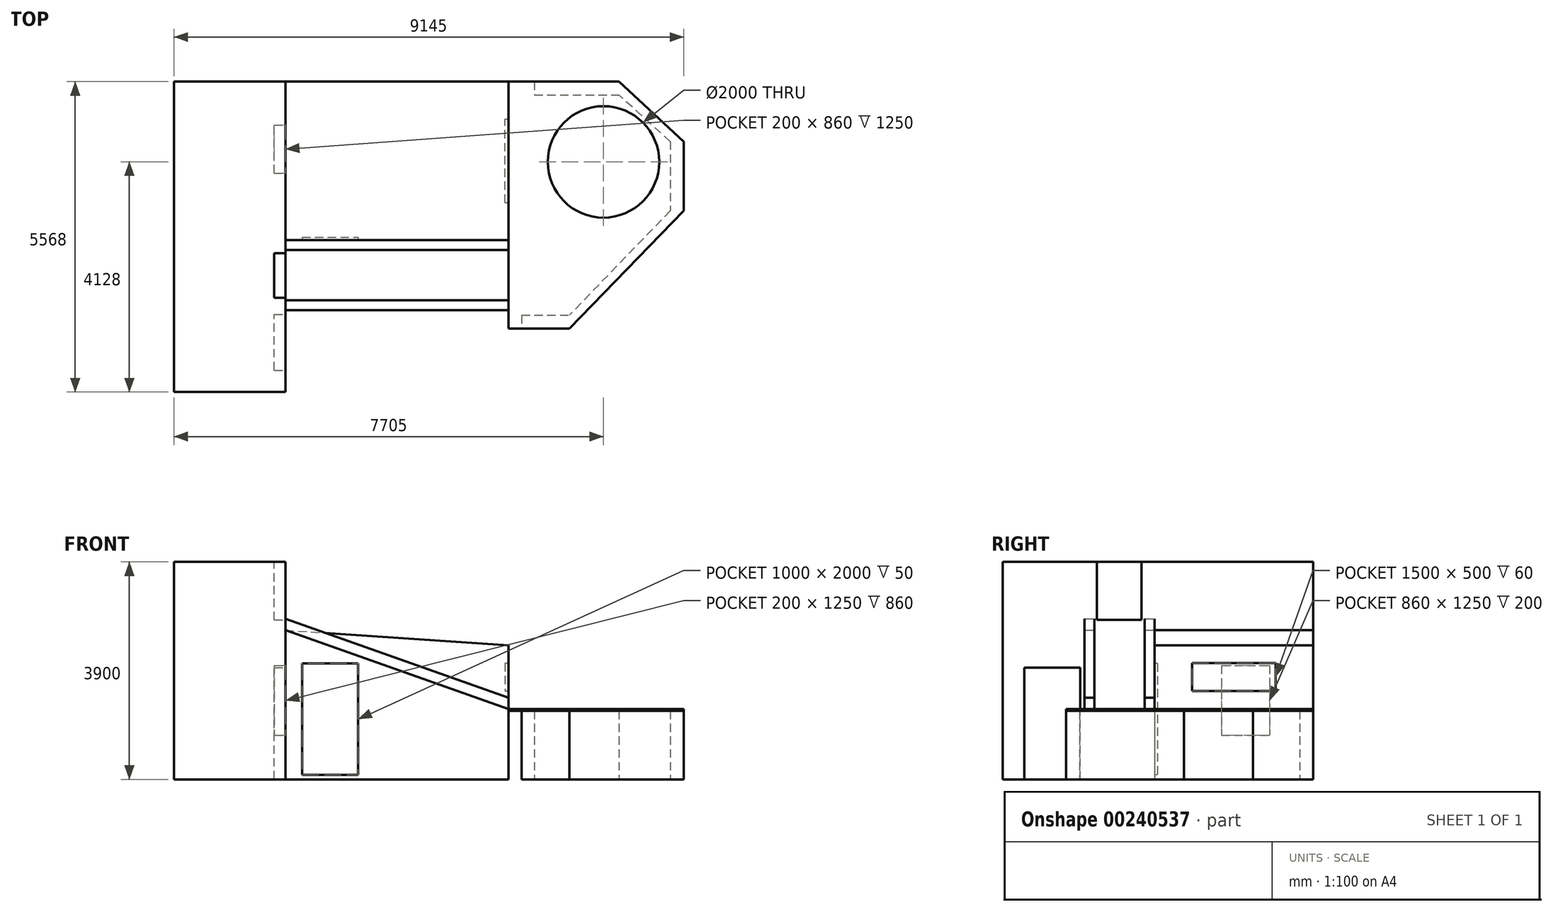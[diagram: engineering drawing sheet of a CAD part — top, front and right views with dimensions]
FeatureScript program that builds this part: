
annotation { "Feature Type Name" : "Feature", "Feature Type Description" : "" }
export const myFeature = defineFeature(function(context is Context, id is Id, definition is map)
    precondition{}
    {
        {
            var Q0;
            Q0=qCreatedBy(makeId("Top.planeOp"),FACE);
            var sketch = newSketch(context, id + "F0", { "sketchPlane" : qUnion([Q0])});
            skLineSegment(sketch, "E0", {"start": v(-7881.86, -2753) * mm, "end": v(-5881.86, -2753) * mm});
            skLineSegment(sketch, "E1", {"start": v(-5881.86, -2753) * mm, "end": v(-5881.86, 2815) * mm});
            skLineSegment(sketch, "E2", {"start": v(-7881.86, 2815) * mm, "end": v(-1415.86, 2815) * mm});
            skLineSegment(sketch, "E3", {"start": v(-1881.86, -25) * mm, "end": v(-5881.86, -25) * mm});
            skLineSegment(sketch, "E4.bottom", {"start": v(-1415.86, 2815) * mm, "end": v(98.14, 2815) * mm});
            skLineSegment(sketch, "E4.top", {"start": v(-1415.86, 2575) * mm, "end": v(98.14, 2575) * mm});
            skLineSegment(sketch, "E4.left", {"start": v(-1415.86, 2815) * mm, "end": v(-1415.86, 2575) * mm});
            skLineSegment(sketch, "E4.right", {"start": v(98.14, 2815) * mm, "end": v(98.14, 2575) * mm});
            skLineSegment(sketch, "E5.bottom", {"start": v(-1644.86, -1375) * mm, "end": v(-788.86, -1375) * mm});
            skLineSegment(sketch, "E5.top", {"start": v(-1644.86, -1615) * mm, "end": v(-788.86, -1615) * mm});
            skLineSegment(sketch, "E5.left", {"start": v(-1644.86, -1375) * mm, "end": v(-1644.86, -1615) * mm});
            skLineSegment(sketch, "E5.right", {"start": v(-788.86, -1375) * mm, "end": v(-788.86, -1615) * mm});
            skLineSegment(sketch, "E6.bottom", {"start": v(1023.14, 1739.54) * mm, "end": v(1263.14, 1739.54) * mm});
            skLineSegment(sketch, "E6.top", {"start": v(1023.14, 496.54) * mm, "end": v(1263.14, 496.54) * mm});
            skLineSegment(sketch, "E6.left", {"start": v(1023.14, 1739.54) * mm, "end": v(1023.14, 496.54) * mm});
            skLineSegment(sketch, "E6.right", {"start": v(1263.14, 1739.54) * mm, "end": v(1263.14, 496.54) * mm});
            skLineSegment(sketch, "E7", {"start": v(1023.14, 496.54) * mm, "end": v(-788.86, -1375) * mm});
            skLineSegment(sketch, "E8", {"start": v(1023.14, 1739.54) * mm, "end": v(98.14, 2575) * mm});
            skLineSegment(sketch, "E9", {"start": v(98.14, 2815) * mm, "end": v(1263.14, 1739.54) * mm});
            skLineSegment(sketch, "E10", {"start": v(1263.14, 496.54) * mm, "end": v(-788.86, -1615) * mm});
            skLineSegment(sketch, "E11", {"start": v(-7881.86, 2815) * mm, "end": v(-7881.86, -2753) * mm});
            skCircle(sketch, "E12", {"center": v(-176.86, 1375) * mm, "radius": 1000 * mm});
            skLineSegment(sketch, "E13", {"start": v(-1881.86, -25) * mm, "end": v(-1881.86, 2815) * mm});
            skSolve(sketch);
        }
        {
            var Q0;
            Q0=makeQuery(id+"F0.imprint","IMPRINT",FACE,{"disambiguationData":[TD([[makeQuery(id+"F0.imprint","IMPRINT",EDGE,{"derivedFrom":sQuery(id+"F0.wireOp",EDGE,"E4.bottom")}),-1.0]])]});
            var Q1;
            Q1=makeQuery(id+"F0.imprint","IMPRINT",FACE,{"disambiguationData":[TD([[makeQuery(id+"F0.imprint","IMPRINT",EDGE,{"derivedFrom":sQuery(id+"F0.wireOp",EDGE,"E6.bottom")}),-1.0]])]});
            var Q2;
            Q2=makeQuery(id+"F0.imprint","IMPRINT",FACE,{"disambiguationData":[TD([[makeQuery(id+"F0.imprint","IMPRINT",EDGE,{"derivedFrom":sQuery(id+"F0.wireOp",EDGE,"E4.right")}),1.0]])]});
            var Q3;
            Q3=makeQuery(id+"F0.imprint","IMPRINT",FACE,{"disambiguationData":[TD([[makeQuery(id+"F0.imprint","IMPRINT",EDGE,{"derivedFrom":sQuery(id+"F0.wireOp",EDGE,"E5.right")}),1.0]])]});
            var Q4;
            Q4=makeQuery(id+"F0.imprint","IMPRINT",FACE,{"disambiguationData":[TD([[makeQuery(id+"F0.imprint","IMPRINT",EDGE,{"derivedFrom":sQuery(id+"F0.wireOp",EDGE,"E5.bottom")}),-1.0]])]});
            extrude(context, id + "F1", {"entities" : qUnion([Q0, Q1, Q2, Q3, Q4]), "depth" : 1230 * mm});
        }
        {
            var Q0;
            {var subQ5=sQuery(id+"F0.wireOp",EDGE,"E0");Q0=makeQuery(id+"F0.imprint","IMPRINT",FACE,{"disambiguationData":[TD([[makeQuery(id+"F0.imprint","IMPRINT",EDGE,{"derivedFrom":subQ5}),1.0]])]});}
            extrude(context, id + "F2", {"entities" : qUnion([Q0]), "depth" : 3900 * mm});
        }
        {
            var Q0;
            Q0=makeQuery(id+"F2.opExtrude","SWEPT_FACE",FACE,{"disambiguationData":[OSD([sQuery(id+"F0.wireOp",EDGE,"E1")])]});
            var sketch = newSketch(context, id + "F3", { "sketchPlane" : qUnion([Q0])});
            skLineSegment(sketch, "E14.bottom", {"start": v(-2363, 0) * mm, "end": v(-1363, 0) * mm});
            skLineSegment(sketch, "E14.top", {"start": v(-2363, 2005) * mm, "end": v(-1363, 2005) * mm});
            skLineSegment(sketch, "E14.left", {"start": v(-2363, 0) * mm, "end": v(-2363, 2005) * mm});
            skLineSegment(sketch, "E14.right", {"start": v(-1363, 0) * mm, "end": v(-1363, 2005) * mm});
            skSolve(sketch);
        }
        {
            var Q0;
            Q0=makeQuery(id+"F3.imprint","IMPRINT",FACE,{"disambiguationData":[TD([[makeQuery(id+"F3.imprint","IMPRINT",EDGE,{"derivedFrom":sQuery(id+"F3.wireOp",EDGE,"E14.bottom")}),1.0]])]});
            extrude(context, id + "F4", {"entities" : qUnion([Q0]), "operationType" : NewBodyOperationType.REMOVE, "oppositeDirection" : true, "depth" : 200 * mm});
        }
        {
            var Q0;
            Q0=makeQuery(id+"F2.opExtrude","SWEPT_FACE",FACE,{"disambiguationData":[OSD([sQuery(id+"F0.wireOp",EDGE,"E1")])]});
            var sketch = newSketch(context, id + "F5", { "sketchPlane" : qUnion([Q0])});
            skLineSegment(sketch, "E15.bottom", {"start": v(1175, 2040) * mm, "end": v(2035, 2040) * mm});
            skLineSegment(sketch, "E15.top", {"start": v(1175, 790) * mm, "end": v(2035, 790) * mm});
            skLineSegment(sketch, "E15.left", {"start": v(1175, 2040) * mm, "end": v(1175, 790) * mm});
            skLineSegment(sketch, "E15.right", {"start": v(2035, 2040) * mm, "end": v(2035, 790) * mm});
            skSolve(sketch);
        }
        {
            var Q0;
            Q0=makeQuery(id+"F5.imprint","IMPRINT",FACE,{"disambiguationData":[TD([[makeQuery(id+"F5.imprint","IMPRINT",EDGE,{"derivedFrom":sQuery(id+"F5.wireOp",EDGE,"E15.bottom")}),-1.0]])]});
            extrude(context, id + "F6", {"entities" : qUnion([Q0]), "operationType" : NewBodyOperationType.REMOVE, "oppositeDirection" : true, "depth" : 200 * mm});
        }
        {
            var Q0;
            Q0=makeQuery(id+"F2.opExtrude","SWEPT_FACE",FACE,{"disambiguationData":[OSD([sQuery(id+"F0.wireOp",EDGE,"E1")])]});
            var sketch = newSketch(context, id + "F7", { "sketchPlane" : qUnion([Q0])});
            skLineSegment(sketch, "E16.bottom", {"start": v(-1063, 2860) * mm, "end": v(-263, 2860) * mm});
            skLineSegment(sketch, "E16.top", {"start": v(-1063, 4865) * mm, "end": v(-263, 4865) * mm});
            skLineSegment(sketch, "E16.left", {"start": v(-1063, 2860) * mm, "end": v(-1063, 4865) * mm});
            skLineSegment(sketch, "E16.right", {"start": v(-263, 2860) * mm, "end": v(-263, 4865) * mm});
            skSolve(sketch);
        }
        {
            var Q0;
            {var subQ0=sQuery(id+"F7.wireOp",EDGE,"E16.bottom");Q0=makeQuery(id+"F7.imprint","IMPRINT",FACE,{"disambiguationData":[TD([[makeQuery(id+"F7.imprint","IMPRINT",EDGE,{"derivedFrom":subQ0}),1.0]])]});}
            extrude(context, id + "F8", {"entities" : qUnion([Q0]), "operationType" : NewBodyOperationType.REMOVE, "oppositeDirection" : true, "depth" : 200 * mm});
        }
        {
            var Q0;
            Q0=makeQuery(id+"F1.opExtrude","CAP_FACE",FACE,{"disambiguationData":[OSD([sQuery(id+"F0.wireOp",EDGE,"E4.bottom"),sQuery(id+"F0.wireOp",EDGE,"E4.top"),sQuery(id+"F0.wireOp",EDGE,"E4.left"),sQuery(id+"F0.wireOp",EDGE,"E5.bottom"),sQuery(id+"F0.wireOp",EDGE,"E5.top"),sQuery(id+"F0.wireOp",EDGE,"E5.left"),sQuery(id+"F0.wireOp",EDGE,"E6.left"),sQuery(id+"F0.wireOp",EDGE,"E6.right"),sQuery(id+"F0.wireOp",EDGE,"E7"),sQuery(id+"F0.wireOp",EDGE,"E8"),sQuery(id+"F0.wireOp",EDGE,"E9"),sQuery(id+"F0.wireOp",EDGE,"E10")])],"isStart":false});
            var sketch = newSketch(context, id + "F9", { "sketchPlane" : qUnion([Q0])});
            skLineSegment(sketch, "E17", {"start": v(98.14, 2815) * mm, "end": v(1263.14, 1739.54) * mm});
            skCircle(sketch, "E18", {"center": v(-176.86, 1375) * mm, "radius": 1000 * mm});
            skLineSegment(sketch, "E19", {"start": v(98.14, 2815) * mm, "end": v(-1881.24, 2815) * mm});
            skLineSegment(sketch, "E20", {"start": v(-1881.24, 2815) * mm, "end": v(-1881.24, -1615) * mm});
            skLineSegment(sketch, "E21", {"start": v(-1881.24, -1615) * mm, "end": v(-788.86, -1615) * mm});
            skLineSegment(sketch, "E22", {"start": v(-1881.24, 2815) * mm, "end": v(98.14, 2815) * mm});
            skLineSegment(sketch, "E23", {"start": v(1263.14, 1739.54) * mm, "end": v(1263.14, 496.54) * mm});
            skLineSegment(sketch, "E24", {"start": v(1263.14, 496.54) * mm, "end": v(-788.86, -1615) * mm});
            skSolve(sketch);
        }
        {
            var Q0;
            {var subQ3=sQuery(id+"F0.wireOp",EDGE,"E3");Q0=makeQuery(id+"F0.imprint","IMPRINT",FACE,{"disambiguationData":[TD([[makeQuery(id+"F0.imprint","IMPRINT",EDGE,{"derivedFrom":subQ3}),-1.0]])]});}
            extrude(context, id + "F10", {"entities" : qUnion([Q0]), "operationType" : NewBodyOperationType.ADD, "depth" : 2676 * mm});
        }
        {
            var Q0;
            Q0=makeQuery(id+"F10.opExtrude","SWEPT_FACE",FACE,{"disambiguationData":[OSD([sQuery(id+"F0.wireOp",EDGE,"E3")])]});
            var sketch = newSketch(context, id + "F11", { "sketchPlane" : qUnion([Q0])});
            skLineSegment(sketch, "E25", {"start": v(-5881.86, 2676) * mm, "end": v(-1881.86, 2406) * mm});
            skLineSegment(sketch, "E26", {"start": v(-1881.86, 2406) * mm, "end": v(-1881.86, 2676) * mm});
            skLineSegment(sketch, "E27", {"start": v(-1881.86, 2676) * mm, "end": v(-5881.86, 2676) * mm});
            skSolve(sketch);
        }
        {
            var Q0;
            Q0=makeQuery(id+"F11.imprint","IMPRINT",FACE,{"disambiguationData":[TD([[makeQuery(id+"F11.imprint","IMPRINT",EDGE,{"derivedFrom":sQuery(id+"F11.wireOp",EDGE,"E25")}),1.0]])]});
            extrude(context, id + "F12", {"entities" : qUnion([Q0]), "operationType" : NewBodyOperationType.REMOVE, "oppositeDirection" : true, "depth" : 3620 * mm});
        }
        {
            var Q0;
            Q0=makeQuery(id+"F9.imprint","IMPRINT",FACE,{"disambiguationData":[TD([[makeQuery(id+"F9.imprint","IMPRINT",EDGE,{"derivedFrom":sQuery(id+"F9.wireOp",EDGE,"E18")}),-1.0]])]});
            var Q1;
            {var subQ2=sQuery(id+"F9.wireOp",EDGE,"E17");Q1=makeQuery(id+"F9.imprint","IMPRINT",FACE,{"disambiguationData":[TD([[makeQuery(id+"F9.imprint","IMPRINT",EDGE,{"derivedFrom":subQ2}),-1.0]])]});}
            extrude(context, id + "F13", {"entities" : qUnion([Q0, Q1]), "depth" : 30 * mm});
        }
        {
            var Q0;
            Q0=makeQuery(id+"F10.opExtrude","SWEPT_FACE",FACE,{"disambiguationData":[OSD([sQuery(id+"F0.wireOp",EDGE,"E3")])]});
            var sketch = newSketch(context, id + "F14", { "sketchPlane" : qUnion([Q0])});
            skLineSegment(sketch, "E28", {"start": v(-5881.86, 2676) * mm, "end": v(-1881.86, 1262.3) * mm});
            skLineSegment(sketch, "E29", {"start": v(-5883.2, 2877.77) * mm, "end": v(-1881.86, 1463.59) * mm});
            skLineSegment(sketch, "E30", {"start": v(-5883.2, 2877.77) * mm, "end": v(-5881.86, 2676) * mm});
            skLineSegment(sketch, "E31", {"start": v(-1881.86, 1262.3) * mm, "end": v(-1881.86, 1463.59) * mm});
            skSolve(sketch);
        }
        {
            var Q0;
            {var subQ0=sQuery(id+"F14.wireOp",EDGE,"E30");Q0=makeQuery(id+"F14.imprint","IMPRINT",FACE,{"disambiguationData":[TD([[makeQuery(id+"F14.imprint","IMPRINT",EDGE,{"derivedFrom":subQ0}),1.0]])]});}
            var Q1;
            {var subQ0=sQuery(id+"F14.wireOp",EDGE,"E28");Q1=makeQuery(id+"F14.imprint","IMPRINT",FACE,{"disambiguationData":[TD([[makeQuery(id+"F14.imprint","IMPRINT",EDGE,{"derivedFrom":subQ0}),1.0]])]});}
            extrude(context, id + "F15", {"entities" : qUnion([Q0, Q1]), "depth" : 180 * mm});
        }
        {
            var Q0;
            Q0=makeQuery(id+"F15.opExtrude","CAP_FACE",FACE,{"disambiguationData":[OSD([sQuery(id+"F14.wireOp",EDGE,"E28"),sQuery(id+"F14.wireOp",EDGE,"E29"),sQuery(id+"F14.wireOp",EDGE,"E30"),sQuery(id+"F14.wireOp",EDGE,"E31")])],"isStart":false});
            var sketch = newSketch(context, id + "F16", { "sketchPlane" : qUnion([Q0])});
            skLineSegment(sketch, "E32", {"start": v(-5883.2, 2877.77) * mm, "end": v(-5881.86, 2676) * mm});
            skLineSegment(sketch, "E33", {"start": v(-5881.86, 2676) * mm, "end": v(-1881.86, 1262.3) * mm});
            skLineSegment(sketch, "E34", {"start": v(-1881.86, 1262.3) * mm, "end": v(-1881.86, 1463.59) * mm});
            skLineSegment(sketch, "E35", {"start": v(-1881.86, 1463.59) * mm, "end": v(-5883.2, 2877.77) * mm});
            skSolve(sketch);
        }
        {
            var Q0;
            Q0=makeQuery(id+"F16.imprint","IMPRINT",FACE,{"disambiguationData":[TD([[makeQuery(id+"F16.imprint","IMPRINT",EDGE,{"derivedFrom":sQuery(id+"F16.wireOp",EDGE,"E32")}),1.0]])]});
            extrude(context, id + "F17", {"entities" : qUnion([Q0]), "depth" : 1080 * mm, "hasSecondDirection" : true, "secondDirectionOppositeDirection" : false, "secondDirectionDepth" : 900 * mm});
        }
        {
            var Q0;
            {var subQ0=sQuery(id+"F14.wireOp",EDGE,"E28");Q0=makeQuery(id+"F14.imprint","IMPRINT",FACE,{"disambiguationData":[TD([[makeQuery(id+"F14.imprint","IMPRINT",EDGE,{"derivedFrom":subQ0}),-1.0]])]});}
            var sketch = newSketch(context, id + "F18", { "sketchPlane" : qUnion([Q0])});
            skLineSegment(sketch, "E36.bottom", {"start": v(-5581.86, 2080) * mm, "end": v(-4581.86, 2080) * mm});
            skLineSegment(sketch, "E36.top", {"start": v(-5581.86, 80) * mm, "end": v(-4581.86, 80) * mm});
            skLineSegment(sketch, "E36.left", {"start": v(-5581.86, 2080) * mm, "end": v(-5581.86, 80) * mm});
            skLineSegment(sketch, "E36.right", {"start": v(-4581.86, 2080) * mm, "end": v(-4581.86, 80) * mm});
            skSolve(sketch);
        }
        {
            var Q0;
            Q0=makeQuery(id+"F18.imprint","IMPRINT",FACE,{"disambiguationData":[TD([[makeQuery(id+"F18.imprint","IMPRINT",EDGE,{"derivedFrom":sQuery(id+"F18.wireOp",EDGE,"E36.bottom")}),-1.0]])]});
            extrude(context, id + "F19", {"entities" : qUnion([Q0]), "operationType" : NewBodyOperationType.REMOVE, "oppositeDirection" : true, "depth" : 50 * mm});
        }
        {
            var Q0;
            Q0=makeQuery(id+"F10.opExtrude","SWEPT_FACE",FACE,{"disambiguationData":[OSD([sQuery(id+"F0.wireOp",EDGE,"E13")])]});
            var sketch = newSketch(context, id + "F20", { "sketchPlane" : qUnion([Q0])});
            skLineSegment(sketch, "E37.bottom", {"start": v(644, 2086) * mm, "end": v(2144, 2086) * mm});
            skLineSegment(sketch, "E37.top", {"start": v(644, 1586) * mm, "end": v(2144, 1586) * mm});
            skLineSegment(sketch, "E37.left", {"start": v(644, 2086) * mm, "end": v(644, 1586) * mm});
            skLineSegment(sketch, "E37.right", {"start": v(2144, 2086) * mm, "end": v(2144, 1586) * mm});
            skSolve(sketch);
        }
        {
            var Q0;
            Q0=makeQuery(id+"F20.imprint","IMPRINT",FACE,{"disambiguationData":[TD([[makeQuery(id+"F20.imprint","IMPRINT",EDGE,{"derivedFrom":sQuery(id+"F20.wireOp",EDGE,"E37.bottom")}),-1.0]])]});
            extrude(context, id + "F21", {"entities" : qUnion([Q0]), "operationType" : NewBodyOperationType.REMOVE, "oppositeDirection" : true, "depth" : 60 * mm});
        }
    });
